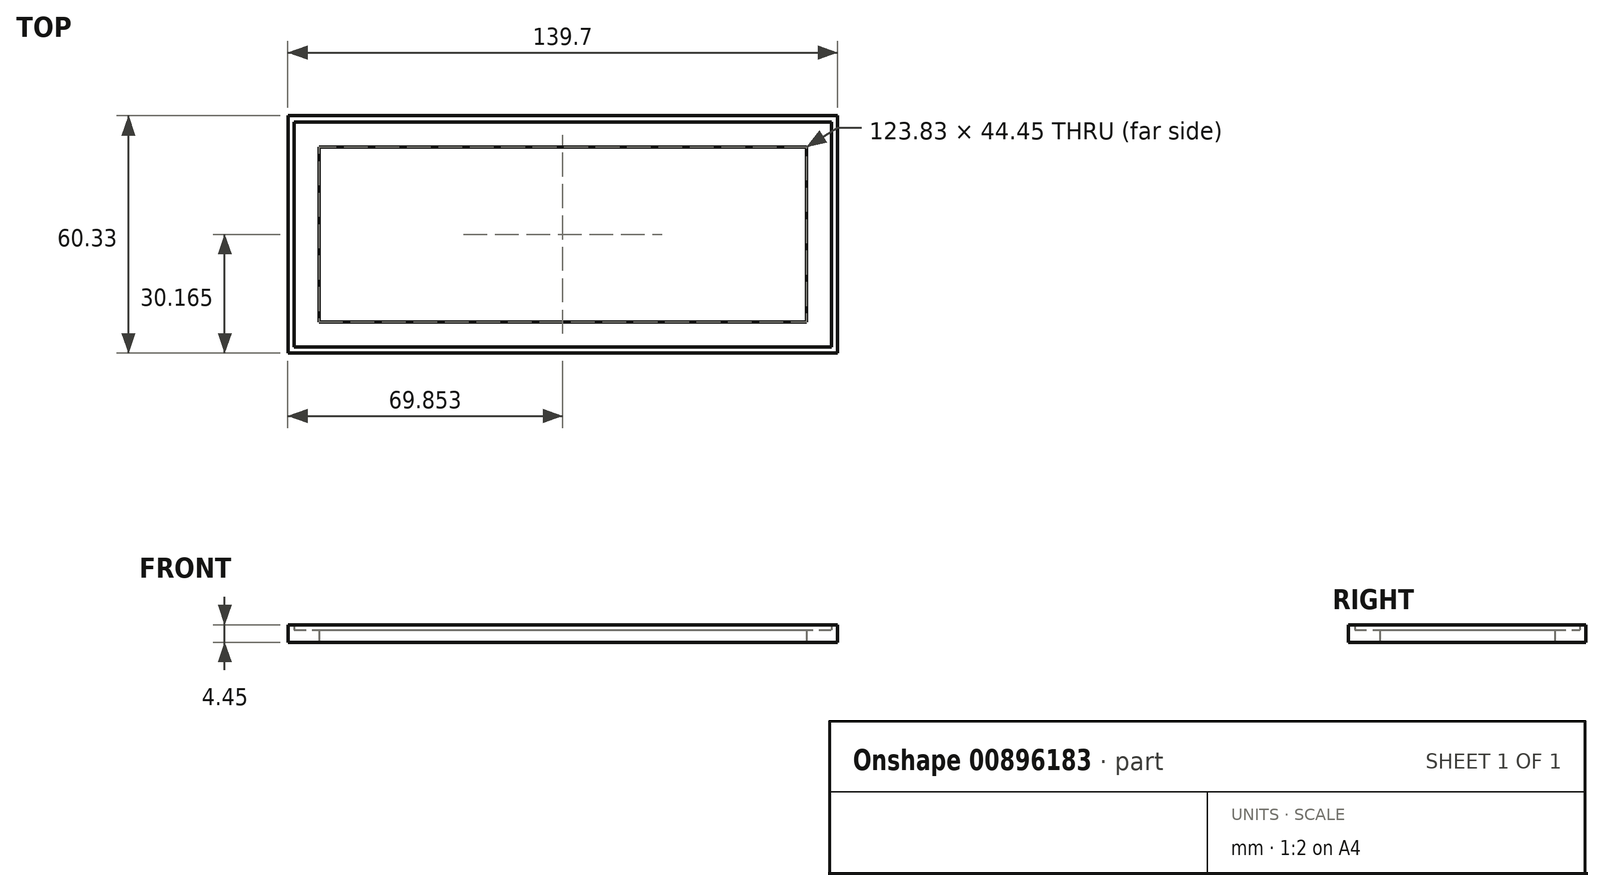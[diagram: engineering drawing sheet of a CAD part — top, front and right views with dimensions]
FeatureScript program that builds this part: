
annotation { "Feature Type Name" : "Feature", "Feature Type Description" : "" }
export const myFeature = defineFeature(function(context is Context, id is Id, definition is map)
    precondition{}
    {
        {
            var Q0;
            Q0=qCreatedBy(makeId("Top.planeOp"),FACE);
            var sketch = newSketch(context, id + "F0", { "sketchPlane" : qUnion([Q0])});
            skLineSegment(sketch, "E0.bottom", {"start": v(0, 0) * mm, "end": v(136.53, 0) * mm});
            skLineSegment(sketch, "E0.top", {"start": v(0, 57.15) * mm, "end": v(136.53, 57.15) * mm});
            skLineSegment(sketch, "E0.left", {"start": v(0, 0) * mm, "end": v(0, 57.15) * mm});
            skLineSegment(sketch, "E0.right", {"start": v(136.53, 0) * mm, "end": v(136.53, 57.15) * mm});
            skLineSegment(sketch, "E1.0", {"start": v(6.35, 6.35) * mm, "end": v(6.35, 50.8) * mm});
            skLineSegment(sketch, "E1.1", {"start": v(6.35, 6.35) * mm, "end": v(130.18, 6.35) * mm});
            skLineSegment(sketch, "E1.2", {"start": v(130.18, 6.35) * mm, "end": v(130.18, 50.8) * mm});
            skLineSegment(sketch, "E1.3", {"start": v(6.35, 50.8) * mm, "end": v(130.18, 50.8) * mm});
            skSolve(sketch);
        }
        {
            var Q0;
            Q0=makeQuery(id+"F0.imprint","IMPRINT",FACE,{"disambiguationData":[TD([[makeQuery(id+"F0.imprint","IMPRINT",EDGE,{"derivedFrom":sQuery(id+"F0.wireOp",EDGE,"E0.bottom")}),1.0]])]});
            extrude(context, id + "F1", {"entities" : qUnion([Q0]), "depth" : 3.17 * mm, "offsetDistance" : 25.4 * mm});
        }
        {
            var Q0;
            Q0=qCreatedBy(makeId("Top.planeOp"),FACE);
            var sketch = newSketch(context, id + "F2", { "sketchPlane" : qUnion([Q0])});
            skLineSegment(sketch, "E2.0", {"start": v(-1.59, 58.74) * mm, "end": v(138.11, 58.74) * mm});
            skLineSegment(sketch, "E2.1", {"start": v(-1.59, -1.59) * mm, "end": v(-1.59, 58.74) * mm});
            skLineSegment(sketch, "E2.2", {"start": v(-1.59, -1.59) * mm, "end": v(138.11, -1.59) * mm});
            skLineSegment(sketch, "E2.3", {"start": v(138.11, -1.59) * mm, "end": v(138.11, 58.74) * mm});
            skLineSegment(sketch, "E3.0", {"start": v(0, 57.15) * mm, "end": v(136.53, 57.15) * mm});
            skLineSegment(sketch, "E3.1", {"start": v(0, 0) * mm, "end": v(0, 57.15) * mm});
            skLineSegment(sketch, "E3.2", {"start": v(0, 0) * mm, "end": v(136.53, 0) * mm});
            skLineSegment(sketch, "E3.3", {"start": v(136.53, 0) * mm, "end": v(136.53, 57.15) * mm});
            skSolve(sketch);
        }
        {
            var Q0;
            Q0=makeQuery(id+"F2.imprint","IMPRINT",FACE,{"disambiguationData":[TD([[makeQuery(id+"F2.imprint","IMPRINT",EDGE,{"derivedFrom":sQuery(id+"F2.wireOp",EDGE,"E2.0")}),-1.0]])]});
            extrude(context, id + "F3", {"entities" : qUnion([Q0]), "operationType" : NewBodyOperationType.ADD, "depth" : 4.44 * mm, "offsetDistance" : 25.4 * mm});
        }
    });
